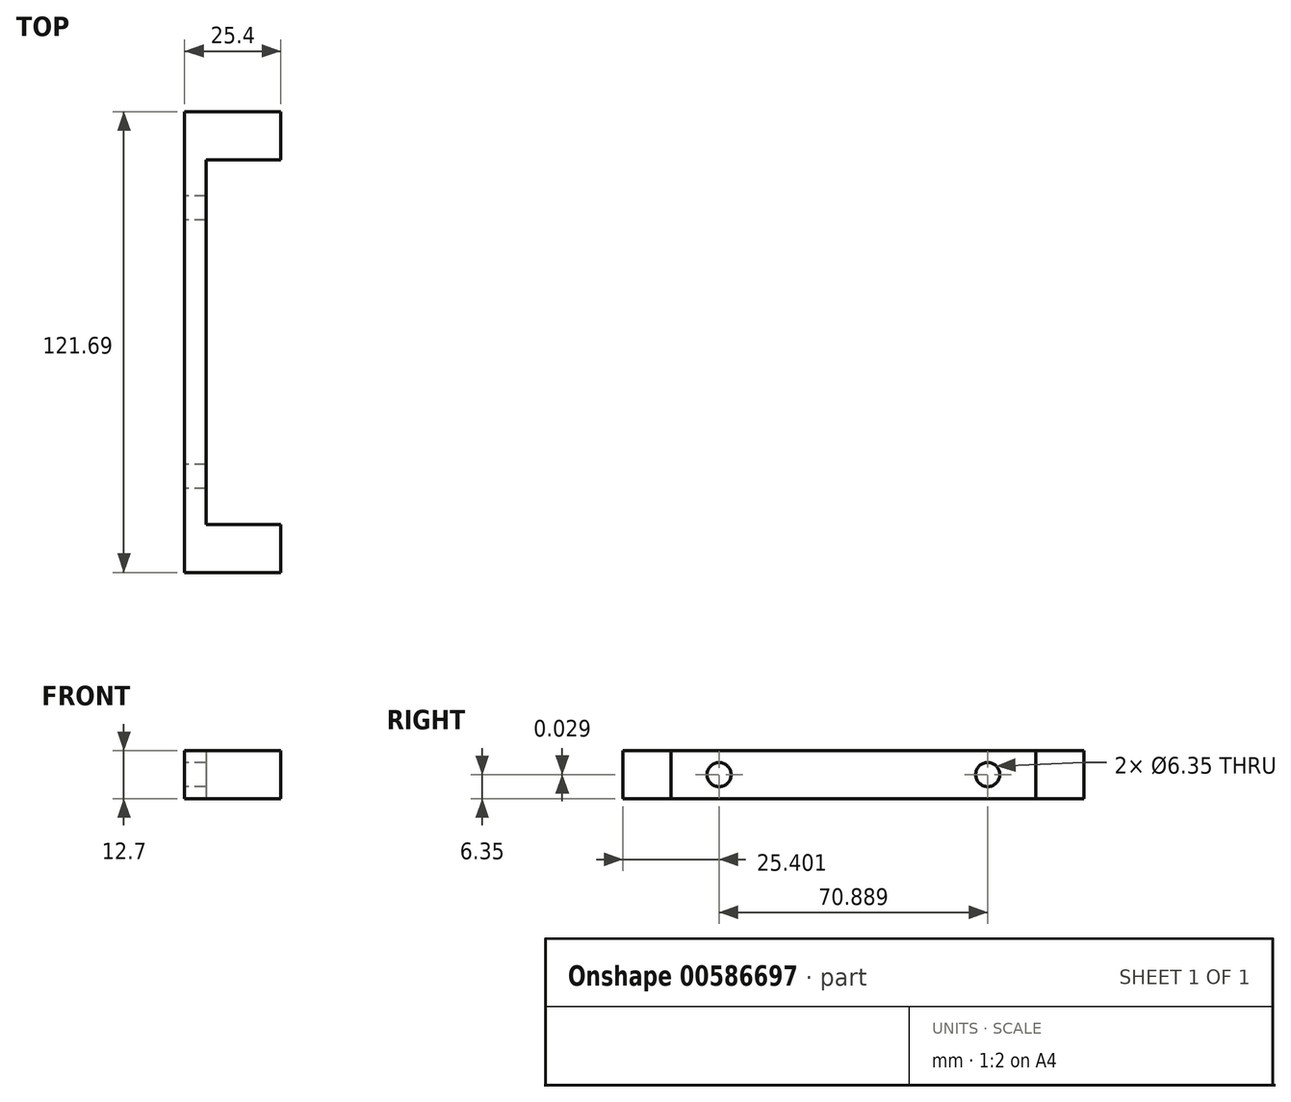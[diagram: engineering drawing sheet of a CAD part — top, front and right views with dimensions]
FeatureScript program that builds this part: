
annotation { "Feature Type Name" : "Feature", "Feature Type Description" : "" }
export const myFeature = defineFeature(function(context is Context, id is Id, definition is map)
    precondition{}
    {
        {
            var Q0;
            Q0=qCreatedBy(makeId("Top.planeOp"),FACE);
            var sketch = newSketch(context, id + "F0", { "sketchPlane" : qUnion([Q0])});
            skLineSegment(sketch, "E0.bottom", {"start": v(-5.95, 58.4) * mm, "end": v(6.06, 58.4) * mm});
            skLineSegment(sketch, "E0.top", {"start": v(-5.95, -63.3) * mm, "end": v(6.06, -63.3) * mm});
            skLineSegment(sketch, "E0.left", {"start": v(-5.95, 58.4) * mm, "end": v(-5.95, -63.3) * mm});
            skLineSegment(sketch, "E0.right", {"start": v(6.06, 45.7) * mm, "end": v(6.06, -50.6) * mm});
            skLineSegment(sketch, "E1.bottom", {"start": v(6.06, 58.4) * mm, "end": v(19.45, 58.4) * mm});
            skLineSegment(sketch, "E1.top", {"start": v(6.06, 45.7) * mm, "end": v(19.45, 45.7) * mm});
            skLineSegment(sketch, "E1.right", {"start": v(19.45, 58.4) * mm, "end": v(19.45, 45.7) * mm});
            skLineSegment(sketch, "E2.bottom", {"start": v(6.06, -50.6) * mm, "end": v(19.45, -50.6) * mm});
            skLineSegment(sketch, "E2.top", {"start": v(6.06, -63.3) * mm, "end": v(19.45, -63.3) * mm});
            skLineSegment(sketch, "E2.right", {"start": v(19.45, -50.6) * mm, "end": v(19.45, -63.3) * mm});
            skSolve(sketch);
        }
        {
            var Q0;
            Q0=makeQuery(id+"F0.imprint","IMPRINT",FACE,{"disambiguationData":[TD([[makeQuery(id+"F0.imprint","IMPRINT",EDGE,{"derivedFrom":sQuery(id+"F0.wireOp",EDGE,"E0.bottom")}),-1.0]])]});
            extrude(context, id + "F1", {"entities" : qUnion([Q0]), "depth" : 12.7 * mm, "offsetDistance" : 25.4 * mm});
        }
        {
            var Q0;
            Q0=makeQuery(id+"F1.opExtrude","SWEPT_FACE",FACE,{"disambiguationData":[OSD([sQuery(id+"F0.wireOp",EDGE,"E0.right")])]});
            extrude(context, id + "F2", {"entities" : qUnion([Q0]), "operationType" : NewBodyOperationType.REMOVE, "oppositeDirection" : true, "depth" : 6.35 * mm, "offsetDistance" : 25.4 * mm});
        }
        {
            var Q0;
            Q0=makeQuery(id+"F2.boolean.opBoolean","COPY",FACE,{"derivedFrom":makeQuery(id+"F2.opExtrude","CAP_FACE",FACE,{"disambiguationData":[OSD([sQuery(id+"F0.wireOp",EDGE,"E0.right")])],"isStart":false})});
            var sketch = newSketch(context, id + "F3", { "sketchPlane" : qUnion([Q0])});
            skCircle(sketch, "E3", {"center": v(-37.9, 6.35) * mm, "radius": 2.54 * mm});
            skCircle(sketch, "E4", {"center": v(33, 6.38) * mm, "radius": 2.54 * mm});
            skSolve(sketch);
        }
        {
            var Q0;
            Q0=sQuery(id+"F3.wireOp",VERTEX,"E4.center");
            var Q1;
            Q1=sQuery(id+"F3.wireOp",VERTEX,"E3.center");
            var Q2;
            Q2=makeQuery(id+"F1.opExtrude","SWEPT_BODY",BODY,{"disambiguationData":[OSD([sQuery(id+"F0.wireOp",EDGE,"E0.bottom"),sQuery(id+"F0.wireOp",EDGE,"E0.top"),sQuery(id+"F0.wireOp",EDGE,"E0.left"),sQuery(id+"F0.wireOp",EDGE,"E0.right"),sQuery(id+"F0.wireOp",EDGE,"E1.bottom"),sQuery(id+"F0.wireOp",EDGE,"E1.top"),sQuery(id+"F0.wireOp",EDGE,"E1.right"),sQuery(id+"F0.wireOp",EDGE,"E2.bottom"),sQuery(id+"F0.wireOp",EDGE,"E2.top"),sQuery(id+"F0.wireOp",EDGE,"E2.right")])]});
            hole(context, id + "F4", {"style" : HoleStyle.SIMPLE, "endStyle" : HoleEndStyle.THROUGH, "holeDiameter" : 6.35 * mm, "majorDiameter" : 6.35 * mm, "isTappedThrough" : true, "tappedDepth" : 12.7 * mm, "tapClearance" : 3, "locations" : qUnion([Q0, Q1]), "scope" : qUnion([Q2]), "startStyle" : HoleStartStyle.PART});
        }
    });
